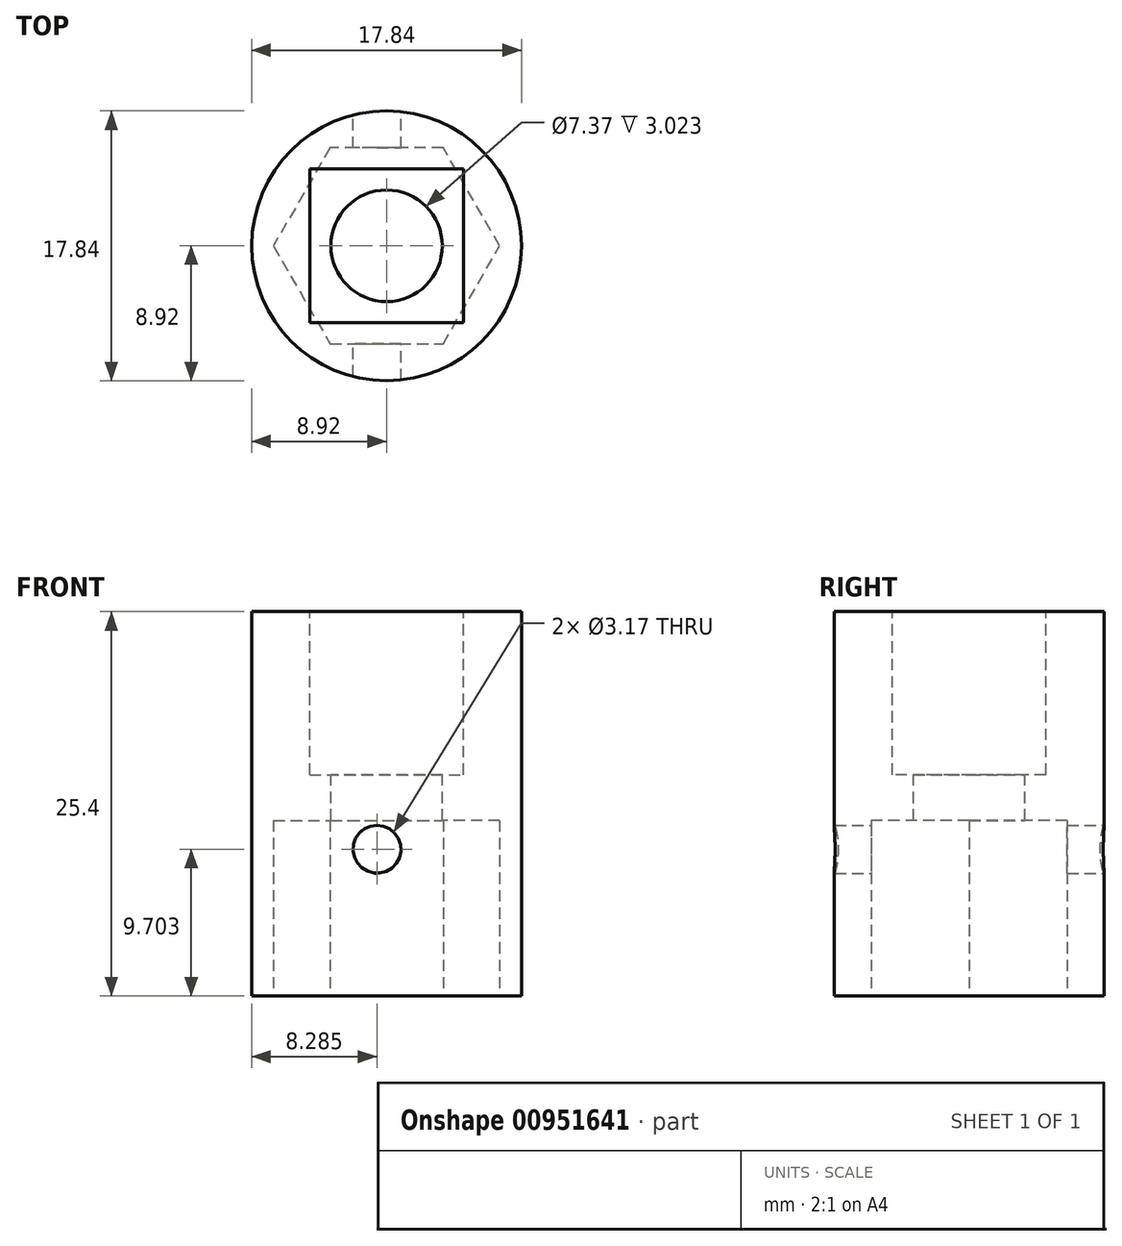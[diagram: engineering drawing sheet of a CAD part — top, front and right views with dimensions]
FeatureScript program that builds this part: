
annotation { "Feature Type Name" : "Feature", "Feature Type Description" : "" }
export const myFeature = defineFeature(function(context is Context, id is Id, definition is map)
    precondition{}
    {
        {
            var Q0;
            Q0=qCreatedBy(makeId("Top.planeOp"),FACE);
            var sketch = newSketch(context, id + "F0", { "sketchPlane" : qUnion([Q0])});
            skCircle(sketch, "E0", {"center": v(0, 0) * mm, "radius": 8.92 * mm});
            skSolve(sketch);
        }
        {
            var Q0;
            Q0 = qSketchRegion(id + "F0", true);
            extrude(context, id + "F1", {"entities" : qUnion([Q0]), "depth" : 25.4 * mm, "offsetDistance" : 25 * mm});
        }
        {
            var Q0;
            Q0=makeQuery(id+"F1.opExtrude","CAP_FACE",FACE,{"disambiguationData":[OSD([sQuery(id+"F0.wireOp",EDGE,"E0")])],"isStart":false});
            var sketch = newSketch(context, id + "F2", { "sketchPlane" : qUnion([Q0])});
            skLineSegment(sketch, "E1.bottom", {"start": v(-5.08, 5.08) * mm, "end": v(5.08, 5.08) * mm});
            skLineSegment(sketch, "E1.top", {"start": v(-5.08, -5.08) * mm, "end": v(5.08, -5.08) * mm});
            skLineSegment(sketch, "E1.left", {"start": v(-5.08, 5.08) * mm, "end": v(-5.08, -5.08) * mm});
            skLineSegment(sketch, "E1.right", {"start": v(5.08, 5.08) * mm, "end": v(5.08, -5.08) * mm});
            skPoint(sketch, "E1.middle", {"position": v(0, 0) * mm});
            skSolve(sketch);
        }
        {
            var Q0;
            Q0 = qSketchRegion(id + "F2", true);
            extrude(context, id + "F3", {"entities" : qUnion([Q0]), "operationType" : NewBodyOperationType.REMOVE, "oppositeDirection" : true, "depth" : 10.77 * mm, "offsetDistance" : 25 * mm});
        }
        {
            var Q0;
            Q0=makeQuery(id+"F3.boolean.opBoolean","COPY",FACE,{"derivedFrom":makeQuery(id+"F3.opExtrude","CAP_FACE",FACE,{"disambiguationData":[OSD([sQuery(id+"F2.wireOp",EDGE,"E1.bottom"),sQuery(id+"F2.wireOp",EDGE,"E1.top"),sQuery(id+"F2.wireOp",EDGE,"E1.left"),sQuery(id+"F2.wireOp",EDGE,"E1.right")])],"isStart":false})});
            var sketch = newSketch(context, id + "F4", { "sketchPlane" : qUnion([Q0])});
            skCircle(sketch, "E2", {"center": v(0, 0) * mm, "radius": 3.68 * mm});
            skSolve(sketch);
        }
        {
            var Q0;
            Q0 = qSketchRegion(id + "F4", true);
            extrude(context, id + "F5", {"entities" : qUnion([Q0]), "operationType" : NewBodyOperationType.REMOVE, "endBound" : BoundingType.THROUGH_ALL, "oppositeDirection" : true, "depth" : 25 * mm, "offsetDistance" : 25 * mm});
        }
        {
            var Q0;
            Q0=makeQuery(id+"F1.opExtrude","CAP_FACE",FACE,{"disambiguationData":[OSD([sQuery(id+"F0.wireOp",EDGE,"E0")])],"isStart":true});
            var sketch = newSketch(context, id + "F6", { "sketchPlane" : qUnion([Q0])});
            skCircle(sketch, "E3.cCircle", {"center": v(0, 0) * mm, "radius": 6.48 * mm, "construction": true});
            skLineSegment(sketch, "E3.0", {"start": v(-3.74, 6.48) * mm, "end": v(3.74, 6.48) * mm});
            skLineSegment(sketch, "E3.1", {"start": v(3.74, 6.48) * mm, "end": v(7.48, 0) * mm});
            skLineSegment(sketch, "E3.2", {"start": v(7.48, 0) * mm, "end": v(3.74, -6.48) * mm});
            skLineSegment(sketch, "E3.3", {"start": v(3.74, -6.48) * mm, "end": v(-3.74, -6.48) * mm});
            skLineSegment(sketch, "E3.4", {"start": v(-3.74, -6.48) * mm, "end": v(-7.48, 0) * mm});
            skLineSegment(sketch, "E3.5", {"start": v(-7.48, 0) * mm, "end": v(-3.74, 6.48) * mm});
            skPoint(sketch, "E3.0.midPoint", {"position": v(0, 6.48) * mm});
            skSolve(sketch);
        }
        {
            var Q0;
            Q0 = qSketchRegion(id + "F6", true);
            extrude(context, id + "F7", {"entities" : qUnion([Q0]), "operationType" : NewBodyOperationType.REMOVE, "oppositeDirection" : true, "depth" : 11.6 * mm, "offsetDistance" : 25.4 * mm});
        }
        {
            var Q0;
            Q0=makeQuery(id+"F7.boolean.opBoolean","COPY",FACE,{"derivedFrom":makeQuery(id+"F7.opExtrude","SWEPT_FACE",FACE,{"disambiguationData":[OSD([sQuery(id+"F6.wireOp",EDGE,"E3.0")])]})});
            var sketch = newSketch(context, id + "F8", { "sketchPlane" : qUnion([Q0])});
            skCircle(sketch, "E4", {"center": v(0.64, 9.7) * mm, "radius": 1.59 * mm});
            skSolve(sketch);
        }
        {
            var Q0;
            Q0 = qSketchRegion(id + "F8", true);
            extrude(context, id + "F9", {"entities" : qUnion([Q0]), "operationType" : NewBodyOperationType.REMOVE, "endBound" : BoundingType.SYMMETRIC, "oppositeDirection" : true, "depth" : 50.8 * mm, "offsetDistance" : 25.4 * mm});
        }
    });
